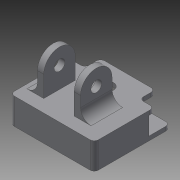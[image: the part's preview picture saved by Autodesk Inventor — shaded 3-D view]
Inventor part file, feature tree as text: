
AUTODESK INVENTOR PART (.ipt)
format: ipt  version: 2013 (Build 170138000, 138)  size: 200,704 bytes
history: native  units: mm
features: extrude x7, sketch x7, fillet x3, mirror x2
ambient origin geometry x8: Origin, YZ Plane, XZ Plane, XY Plane, X Axis, Y Axis, Z Axis, Center Point
bodies: Solid1 (feature_tree)
feature tree (19):
  extrude  "Extrusion1"  Depth=6.35mm
  extrude  "Extrusion2"  Depth=10.0mm
  extrude  "Extrusion3"  Depth=8.5mm TaperAngle=0.0deg
  mirror  "Mirror1"
  extrude  "Extrusion4"  Depth=2.0mm TaperAngle=0.0deg
  mirror  "Mirror2"
  extrude  "Extrusion5"  Depth=2.0mm TaperAngle=0.0deg
  extrude  "Extrusion6"  Depth=12.5mm
  extrude  "Extrusion7"  Depth=12.5mm
  fillet  "Fillet1"  Radius=16.0mm
  fillet  "Fillet2"  Radius=15.0mm
  fillet  "Fillet3"  Radius=3.0mm
  sketch  "Sketch1"  dims[d0=40.0mm d2=6.35mm]
  sketch  "Sketch2"  dims[d4=9.5mm d5=10.0mm]
  sketch  "Sketch4"  dims[d6=20.0mm d7=8.5mm d8=0.0mm]
  sketch  "Sketch5"  dims[d9=20.0mm d10=2.0mm d11=0.0mm]
  sketch  "Sketch6"  dims[d12=6.35mm d13=2.0mm d14=0.0mm]
  sketch  "Sketch7"  dims[d15=7.0mm d17=12.5mm]
  sketch  "Sketch8"  dims[d18=2.0mm d19=0.0mm d20=12.5mm d21=16.0mm d22=0.0mm d23=15.0mm d25=3.0mm d27=5.0mm d28=14.5mm d29=17.5mm d30=0.0mm d31=5.1mm d34=7.5mm d35=10.0mm d36=0.0mm d37=7.5mm d38=4.5mm d39=5.0mm d40=2.0mm]
